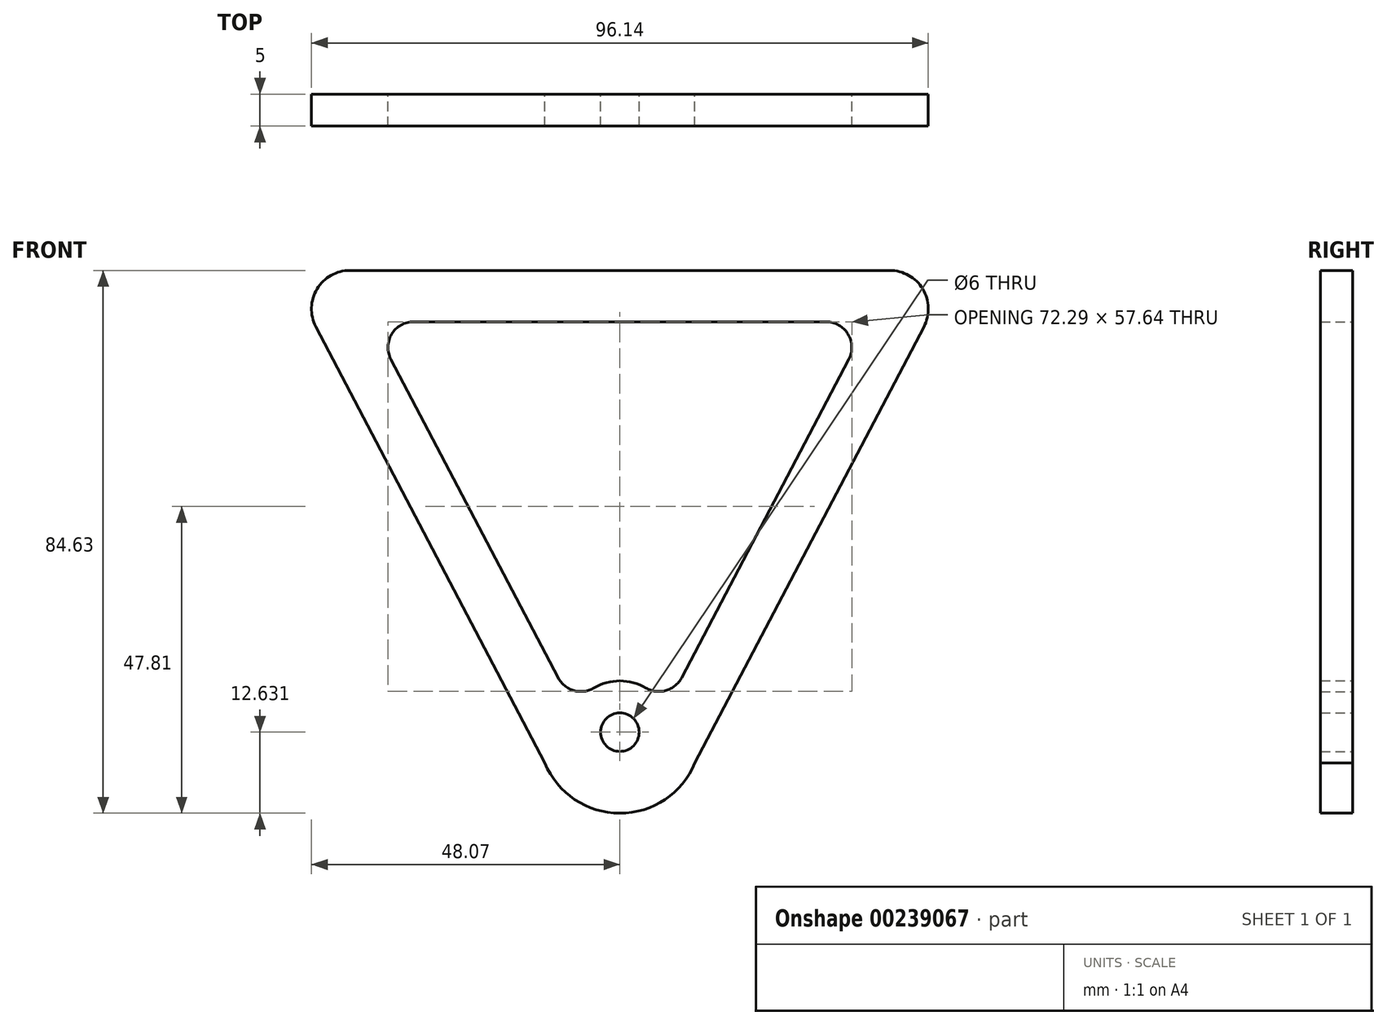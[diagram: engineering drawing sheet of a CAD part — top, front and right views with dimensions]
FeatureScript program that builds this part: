
annotation { "Feature Type Name" : "Feature", "Feature Type Description" : "" }
export const myFeature = defineFeature(function(context is Context, id is Id, definition is map)
    precondition{}
    {
        {
            var Q0;
            Q0=qCreatedBy(makeId("Front.planeOp"),FACE);
            var sketch = newSketch(context, id + "F0", { "sketchPlane" : qUnion([Q0])});
            skLineSegment(sketch, "E0.bottom", {"start": v(-42.07, 42.9) * mm, "end": v(42.07, 42.9) * mm});
            skLineSegment(sketch, "E1", {"start": v(-47.39, 34.11) * mm, "end": v(-11.69, -33.89) * mm});
            skLineSegment(sketch, "E2", {"start": v(11.69, -33.89) * mm, "end": v(47.39, 34.11) * mm});
            skPoint(sketch, "E3.center.orphan", {"position": v(0, -37.1) * mm});
            skPoint(sketch, "E0.right.end.orphan", {"position": v(52, -37.1) * mm});
            skPoint(sketch, "E0.left.end.orphan", {"position": v(-52, -37.1) * mm});
            skPoint(sketch, "E4.visualSharp", {"position": v(-52, 42.9) * mm});
            skArc(sketch, "E4.filletArc", {"start": v(-42.07, 42.9) * mm, "mid": v(-47.2, 40) * mm, "end": v(-47.39, 34.11) * mm});
            skPoint(sketch, "E5.visualSharp", {"position": v(52, 42.9) * mm});
            skArc(sketch, "E5.filletArc", {"start": v(47.39, 34.11) * mm, "mid": v(47.2, 40) * mm, "end": v(42.07, 42.9) * mm});
            skPoint(sketch, "E6.visualSharp", {"position": v(-10, -37.1) * mm});
            skPoint(sketch, "E7.visualSharp", {"position": v(10, -37.1) * mm});
            skLineSegment(sketch, "E8.1", {"start": v(-35.69, 29.04) * mm, "end": v(-9.62, -20.61) * mm});
            skLineSegment(sketch, "E8.2", {"start": v(-32.15, 34.9) * mm, "end": v(32.15, 34.9) * mm});
            skLineSegment(sketch, "E8.3", {"start": v(9.62, -20.61) * mm, "end": v(35.69, 29.04) * mm});
            skPoint(sketch, "E9.visualSharp", {"position": v(-38.76, 34.9) * mm});
            skArc(sketch, "E9.filletArc", {"start": v(-32.15, 34.9) * mm, "mid": v(-35.57, 32.97) * mm, "end": v(-35.69, 29.04) * mm});
            skPoint(sketch, "E10.visualSharp", {"position": v(38.76, 34.9) * mm});
            skArc(sketch, "E10.filletArc", {"start": v(35.69, 29.04) * mm, "mid": v(35.57, 32.97) * mm, "end": v(32.15, 34.9) * mm});
            skArc(sketch, "E11", {"start": v(4.05, -22.2) * mm, "mid": v(0, -21.1) * mm, "end": v(-4.05, -22.2) * mm});
            skPoint(sketch, "E12.orphan", {"position": v(-5.16, -29.1) * mm});
            skPoint(sketch, "E13.orphan", {"position": v(5.16, -29.1) * mm});
            skCircle(sketch, "E14", {"center": v(0, -29.1) * mm, "radius": 3 * mm});
            skArc(sketch, "E15", {"start": v(-11.69, -33.89) * mm, "mid": v(0, -41.73) * mm, "end": v(11.69, -33.89) * mm});
            skPoint(sketch, "E16.visualSharp", {"position": v(-7.1, -25.41) * mm});
            skArc(sketch, "E16.filletArc", {"start": v(-9.62, -20.61) * mm, "mid": v(-7.18, -22.6) * mm, "end": v(-4.05, -22.2) * mm});
            skPoint(sketch, "E17.visualSharp", {"position": v(7.1, -25.41) * mm});
            skArc(sketch, "E17.filletArc", {"start": v(4.05, -22.2) * mm, "mid": v(7.18, -22.6) * mm, "end": v(9.62, -20.61) * mm});
            skSolve(sketch);
        }
        {
            var Q0;
            Q0=makeQuery(id+"F0.imprint","IMPRINT",FACE,{"disambiguationData":[TD([[makeQuery(id+"F0.imprint","IMPRINT",EDGE,{"derivedFrom":sQuery(id+"F0.wireOp",EDGE,"E0.bottom")}),-1.0]])]});
            extrude(context, id + "F1", {"entities" : qUnion([Q0]), "depth" : 5 * mm, "offsetDistance" : 25 * mm});
        }
    });
